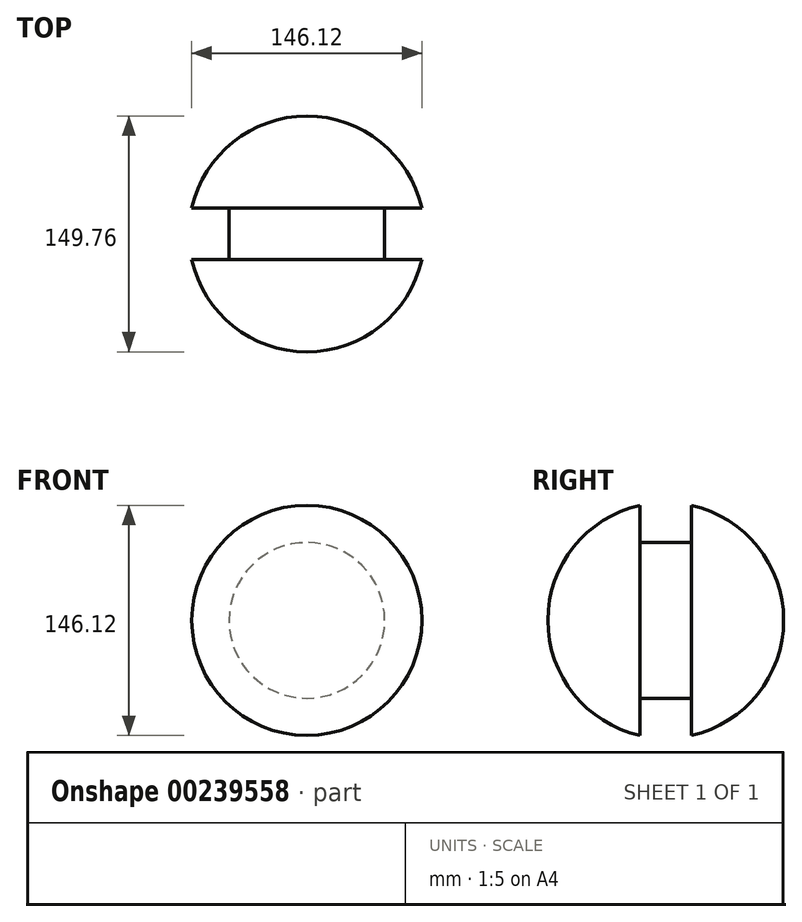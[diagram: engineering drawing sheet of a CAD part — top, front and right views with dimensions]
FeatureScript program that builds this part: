
annotation { "Feature Type Name" : "Feature", "Feature Type Description" : "" }
export const myFeature = defineFeature(function(context is Context, id is Id, definition is map)
    precondition{}
    {
        {
            var Q0;
            Q0=qCreatedBy(makeId("Right.planeOp"),FACE);
            var sketch = newSketch(context, id + "F0", { "sketchPlane" : qUnion([Q0])});
            skArc(sketch, "E0", {"start": v(0, -74.88) * mm, "mid": v(74.88, 0) * mm, "end": v(0, 74.88) * mm});
            skLineSegment(sketch, "E1", {"start": v(0, 74.88) * mm, "end": v(0, -74.88) * mm});
            skSolve(sketch);
        }
        {
            var Q0;
            Q0 = qSketchRegion(id + "F0", true);
            var Q1;
            Q1=sQuery(id+"F0.wireOp",EDGE,"E1");
            revolve(context, id + "F1", {"entities" : qUnion([Q0]), "axis" : qUnion([Q1]), "revolveType" : RevolveType.FULL});
        }
        {
            var Q0;
            Q0=qCreatedBy(makeId("Top.planeOp"),FACE);
            var sketch = newSketch(context, id + "F2", { "sketchPlane" : qUnion([Q0])});
            skLineSegment(sketch, "E2.bottom", {"start": v(49.44, -16.39) * mm, "end": v(111.17, -16.39) * mm});
            skLineSegment(sketch, "E2.top", {"start": v(49.44, 16.39) * mm, "end": v(111.17, 16.39) * mm});
            skLineSegment(sketch, "E2.left", {"start": v(49.44, -16.39) * mm, "end": v(49.44, 16.39) * mm});
            skLineSegment(sketch, "E2.right", {"start": v(111.17, -16.39) * mm, "end": v(111.17, 16.39) * mm});
            skSolve(sketch);
        }
        {
            var Q0;
            Q0=qCreatedBy(makeId("Top.planeOp"),FACE);
            var sketch = newSketch(context, id + "F3", { "sketchPlane" : qUnion([Q0])});
            skLineSegment(sketch, "E3", {"start": v(0, -74.85) * mm, "end": v(0, 74.69) * mm, "construction": true});
            skSolve(sketch);
        }
        {
            var Q0;
            Q0 = qSketchRegion(id + "F3", true);
            var Q1;
            Q1=makeQuery(id+"F2.imprint","IMPRINT",FACE,{"disambiguationData":[TD([[makeQuery(id+"F2.imprint","IMPRINT",EDGE,{"derivedFrom":sQuery(id+"F2.wireOp",EDGE,"E2.bottom")}),1.0]])]});
            var Q2;
            Q2=sQuery(id+"F3.wireOp",EDGE,"E3");
            revolve(context, id + "F4", {"operationType" : NewBodyOperationType.REMOVE, "entities" : qUnion([Q0, Q1]), "axis" : qUnion([Q2]), "revolveType" : RevolveType.FULL, "oppositeDirection" : true});
        }
    });
